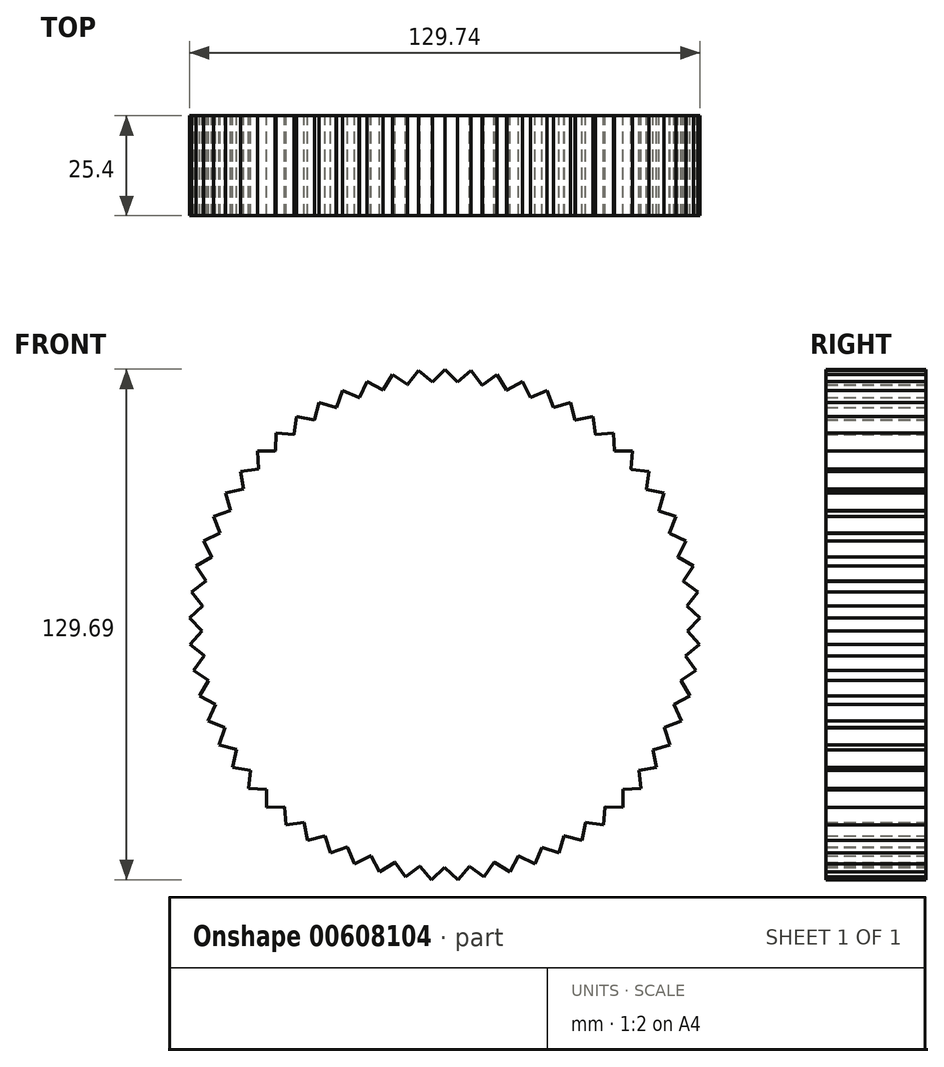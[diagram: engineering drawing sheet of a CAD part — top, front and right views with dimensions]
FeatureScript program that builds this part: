
annotation { "Feature Type Name" : "Feature", "Feature Type Description" : "" }
export const myFeature = defineFeature(function(context is Context, id is Id, definition is map)
    precondition{}
    {
        {
            var Q0;
            Q0=qCreatedBy(makeId("Front.planeOp"),FACE);
            var sketch = newSketch(context, id + "F0", { "sketchPlane" : qUnion([Q0])});
            skCircle(sketch, "E0", {"center": v(0, 0) * mm, "radius": 61.69 * mm});
            skPoint(sketch, "E1", {"position": v(0, -64.89) * mm});
            skPoint(sketch, "E2", {"position": v(65.93, 0) * mm});
            skPoint(sketch, "E3", {"position": v(-64.89, 0) * mm});
            skLineSegment(sketch, "E4", {"start": v(-3.17, 61.56) * mm, "end": v(0, 64.89) * mm});
            skLineSegment(sketch, "E5", {"start": v(0, 64.89) * mm, "end": v(3.18, 61.6) * mm});
            skLineSegment(sketch, "E6.1.0", {"start": v(-9.48, 60.9) * mm, "end": v(-6.67, 64.55) * mm});
            skLineSegment(sketch, "E6.1.1", {"start": v(-6.67, 64.55) * mm, "end": v(-3.17, 61.6) * mm});
            skLineSegment(sketch, "E6.2.0", {"start": v(-15.7, 59.6) * mm, "end": v(-13.27, 63.52) * mm});
            skLineSegment(sketch, "E6.2.1", {"start": v(-13.27, 63.52) * mm, "end": v(-9.5, 60.95) * mm});
            skLineSegment(sketch, "E6.3.0", {"start": v(-21.74, 57.68) * mm, "end": v(-19.73, 61.82) * mm});
            skLineSegment(sketch, "E6.3.1", {"start": v(-19.73, 61.82) * mm, "end": v(-15.7, 59.65) * mm});
            skLineSegment(sketch, "E6.4.0", {"start": v(-27.56, 55.14) * mm, "end": v(-25.98, 59.46) * mm});
            skLineSegment(sketch, "E6.4.1", {"start": v(-25.98, 59.46) * mm, "end": v(-21.76, 57.72) * mm});
            skLineSegment(sketch, "E6.5.0", {"start": v(-33.08, 52.01) * mm, "end": v(-31.96, 56.48) * mm});
            skLineSegment(sketch, "E6.5.1", {"start": v(-31.96, 56.48) * mm, "end": v(-27.58, 55.18) * mm});
            skLineSegment(sketch, "E6.6.0", {"start": v(-38.25, 48.33) * mm, "end": v(-37.6, 52.9) * mm});
            skLineSegment(sketch, "E6.6.1", {"start": v(-37.6, 52.9) * mm, "end": v(-33.1, 52.05) * mm});
            skLineSegment(sketch, "E6.7.0", {"start": v(-43.02, 44.14) * mm, "end": v(-42.83, 48.74) * mm});
            skLineSegment(sketch, "E6.7.1", {"start": v(-42.83, 48.74) * mm, "end": v(-38.28, 48.37) * mm});
            skLineSegment(sketch, "E6.8.0", {"start": v(-47.33, 39.49) * mm, "end": v(-47.62, 44.08) * mm});
            skLineSegment(sketch, "E6.8.1", {"start": v(-47.62, 44.08) * mm, "end": v(-43.05, 44.18) * mm});
            skLineSegment(sketch, "E6.9.0", {"start": v(-51.14, 34.41) * mm, "end": v(-51.9, 38.95) * mm});
            skLineSegment(sketch, "E6.9.1", {"start": v(-51.9, 38.95) * mm, "end": v(-47.37, 39.52) * mm});
            skLineSegment(sketch, "E6.10.0", {"start": v(-54.4, 28.97) * mm, "end": v(-55.63, 33.4) * mm});
            skLineSegment(sketch, "E6.10.1", {"start": v(-55.63, 33.4) * mm, "end": v(-51.18, 34.44) * mm});
            skLineSegment(sketch, "E6.11.0", {"start": v(-57.1, 23.22) * mm, "end": v(-58.77, 27.51) * mm});
            skLineSegment(sketch, "E6.11.1", {"start": v(-58.77, 27.51) * mm, "end": v(-54.45, 29) * mm});
            skLineSegment(sketch, "E6.12.0", {"start": v(-59.18, 17.23) * mm, "end": v(-61.29, 21.32) * mm});
            skLineSegment(sketch, "E6.12.1", {"start": v(-61.29, 21.32) * mm, "end": v(-57.14, 23.24) * mm});
            skLineSegment(sketch, "E6.13.0", {"start": v(-60.64, 11.05) * mm, "end": v(-63.15, 14.91) * mm});
            skLineSegment(sketch, "E6.13.1", {"start": v(-63.15, 14.91) * mm, "end": v(-59.23, 17.24) * mm});
            skLineSegment(sketch, "E6.14.0", {"start": v(-61.46, 4.76) * mm, "end": v(-64.35, 8.34) * mm});
            skLineSegment(sketch, "E6.14.1", {"start": v(-64.35, 8.34) * mm, "end": v(-60.69, 11.06) * mm});
            skLineSegment(sketch, "E6.15.0", {"start": v(-61.62, -1.59) * mm, "end": v(-64.87, 1.68) * mm});
            skLineSegment(sketch, "E6.15.1", {"start": v(-64.87, 1.68) * mm, "end": v(-61.5, 4.76) * mm});
            skLineSegment(sketch, "E6.16.0", {"start": v(-61.13, -7.91) * mm, "end": v(-64.7, -5) * mm});
            skLineSegment(sketch, "E6.16.1", {"start": v(-64.7, -5) * mm, "end": v(-61.67, -1.59) * mm});
            skLineSegment(sketch, "E6.17.0", {"start": v(-60, -14.16) * mm, "end": v(-63.84, -11.63) * mm});
            skLineSegment(sketch, "E6.17.1", {"start": v(-63.84, -11.63) * mm, "end": v(-61.18, -7.92) * mm});
            skLineSegment(sketch, "E6.18.0", {"start": v(-58.22, -20.25) * mm, "end": v(-62.3, -18.13) * mm});
            skLineSegment(sketch, "E6.18.1", {"start": v(-62.3, -18.13) * mm, "end": v(-60.04, -14.17) * mm});
            skLineSegment(sketch, "E6.19.0", {"start": v(-55.83, -26.13) * mm, "end": v(-60.11, -24.44) * mm});
            skLineSegment(sketch, "E6.19.1", {"start": v(-60.11, -24.44) * mm, "end": v(-58.26, -20.27) * mm});
            skLineSegment(sketch, "E6.20.0", {"start": v(-52.84, -31.73) * mm, "end": v(-57.28, -30.5) * mm});
            skLineSegment(sketch, "E6.20.1", {"start": v(-57.28, -30.5) * mm, "end": v(-55.87, -26.15) * mm});
            skLineSegment(sketch, "E6.21.0", {"start": v(-49.3, -37) * mm, "end": v(-53.84, -36.22) * mm});
            skLineSegment(sketch, "E6.21.1", {"start": v(-53.84, -36.22) * mm, "end": v(-52.89, -31.75) * mm});
            skLineSegment(sketch, "E6.22.0", {"start": v(-45.24, -41.87) * mm, "end": v(-49.83, -41.56) * mm});
            skLineSegment(sketch, "E6.22.1", {"start": v(-49.83, -41.56) * mm, "end": v(-49.34, -37.02) * mm});
            skLineSegment(sketch, "E6.23.0", {"start": v(-40.7, -46.3) * mm, "end": v(-45.3, -46.47) * mm});
            skLineSegment(sketch, "E6.23.1", {"start": v(-45.3, -46.47) * mm, "end": v(-45.27, -41.9) * mm});
            skLineSegment(sketch, "E6.24.0", {"start": v(-35.72, -50.24) * mm, "end": v(-40.28, -50.88) * mm});
            skLineSegment(sketch, "E6.24.1", {"start": v(-40.28, -50.88) * mm, "end": v(-40.72, -46.33) * mm});
            skLineSegment(sketch, "E6.25.0", {"start": v(-30.36, -53.64) * mm, "end": v(-34.83, -54.75) * mm});
            skLineSegment(sketch, "E6.25.1", {"start": v(-34.83, -54.75) * mm, "end": v(-35.74, -50.28) * mm});
            skLineSegment(sketch, "E6.26.0", {"start": v(-24.68, -56.48) * mm, "end": v(-29.02, -58.04) * mm});
            skLineSegment(sketch, "E6.26.1", {"start": v(-29.02, -58.04) * mm, "end": v(-30.39, -53.68) * mm});
            skLineSegment(sketch, "E6.27.0", {"start": v(-18.75, -58.72) * mm, "end": v(-22.9, -60.72) * mm});
            skLineSegment(sketch, "E6.27.1", {"start": v(-22.9, -60.72) * mm, "end": v(-24.7, -56.52) * mm});
            skLineSegment(sketch, "E6.28.0", {"start": v(-12.6, -60.34) * mm, "end": v(-16.53, -62.75) * mm});
            skLineSegment(sketch, "E6.28.1", {"start": v(-16.53, -62.75) * mm, "end": v(-18.76, -58.77) * mm});
            skLineSegment(sketch, "E6.29.0", {"start": v(-6.34, -61.31) * mm, "end": v(-10, -64.12) * mm});
            skLineSegment(sketch, "E6.29.1", {"start": v(-10, -64.12) * mm, "end": v(-12.62, -60.38) * mm});
            skLineSegment(sketch, "E6.30.0", {"start": v(0, -61.64) * mm, "end": v(-3.35, -64.8) * mm});
            skLineSegment(sketch, "E6.30.1", {"start": v(-3.35, -64.8) * mm, "end": v(-6.34, -61.36) * mm});
            skLineSegment(sketch, "E6.31.0", {"start": v(6.34, -61.31) * mm, "end": v(3.33, -64.8) * mm});
            skLineSegment(sketch, "E6.31.1", {"start": v(3.33, -64.8) * mm, "end": v(0, -61.69) * mm});
            skLineSegment(sketch, "E6.32.0", {"start": v(12.6, -60.34) * mm, "end": v(9.98, -64.12) * mm});
            skLineSegment(sketch, "E6.32.1", {"start": v(9.98, -64.12) * mm, "end": v(6.34, -61.36) * mm});
            skLineSegment(sketch, "E6.33.0", {"start": v(18.74, -58.72) * mm, "end": v(16.52, -62.75) * mm});
            skLineSegment(sketch, "E6.33.1", {"start": v(16.52, -62.75) * mm, "end": v(12.62, -60.38) * mm});
            skLineSegment(sketch, "E6.34.0", {"start": v(24.68, -56.48) * mm, "end": v(22.88, -60.72) * mm});
            skLineSegment(sketch, "E6.34.1", {"start": v(22.88, -60.72) * mm, "end": v(18.76, -58.77) * mm});
            skLineSegment(sketch, "E6.35.0", {"start": v(30.36, -53.64) * mm, "end": v(29, -58.05) * mm});
            skLineSegment(sketch, "E6.35.1", {"start": v(29, -58.05) * mm, "end": v(24.7, -56.53) * mm});
            skLineSegment(sketch, "E6.36.0", {"start": v(35.71, -50.24) * mm, "end": v(34.82, -54.76) * mm});
            skLineSegment(sketch, "E6.36.1", {"start": v(34.82, -54.76) * mm, "end": v(30.38, -53.69) * mm});
            skLineSegment(sketch, "E6.37.0", {"start": v(40.7, -46.3) * mm, "end": v(40.27, -50.88) * mm});
            skLineSegment(sketch, "E6.37.1", {"start": v(40.27, -50.88) * mm, "end": v(35.74, -50.28) * mm});
            skLineSegment(sketch, "E6.38.0", {"start": v(45.24, -41.87) * mm, "end": v(45.28, -46.47) * mm});
            skLineSegment(sketch, "E6.38.1", {"start": v(45.28, -46.47) * mm, "end": v(40.72, -46.34) * mm});
            skLineSegment(sketch, "E6.39.0", {"start": v(49.3, -37) * mm, "end": v(49.82, -41.57) * mm});
            skLineSegment(sketch, "E6.39.1", {"start": v(49.82, -41.57) * mm, "end": v(45.27, -41.9) * mm});
            skLineSegment(sketch, "E6.40.0", {"start": v(52.84, -31.73) * mm, "end": v(53.83, -36.23) * mm});
            skLineSegment(sketch, "E6.40.1", {"start": v(53.83, -36.23) * mm, "end": v(49.34, -37.03) * mm});
            skLineSegment(sketch, "E6.41.0", {"start": v(55.83, -26.13) * mm, "end": v(57.27, -30.5) * mm});
            skLineSegment(sketch, "E6.41.1", {"start": v(57.27, -30.5) * mm, "end": v(52.88, -31.76) * mm});
            skLineSegment(sketch, "E6.42.0", {"start": v(58.22, -20.25) * mm, "end": v(60.1, -24.45) * mm});
            skLineSegment(sketch, "E6.42.1", {"start": v(60.1, -24.45) * mm, "end": v(55.87, -26.15) * mm});
            skLineSegment(sketch, "E6.43.0", {"start": v(60, -14.16) * mm, "end": v(62.3, -18.14) * mm});
            skLineSegment(sketch, "E6.43.1", {"start": v(62.3, -18.14) * mm, "end": v(58.26, -20.27) * mm});
            skLineSegment(sketch, "E6.44.0", {"start": v(61.13, -7.92) * mm, "end": v(63.84, -11.64) * mm});
            skLineSegment(sketch, "E6.44.1", {"start": v(63.84, -11.64) * mm, "end": v(60.04, -14.17) * mm});
            skLineSegment(sketch, "E6.45.0", {"start": v(61.62, -1.59) * mm, "end": v(64.7, -5.01) * mm});
            skLineSegment(sketch, "E6.45.1", {"start": v(64.7, -5.01) * mm, "end": v(61.18, -7.92) * mm});
            skLineSegment(sketch, "E6.46.0", {"start": v(61.46, 4.76) * mm, "end": v(64.87, 1.66) * mm});
            skLineSegment(sketch, "E6.46.1", {"start": v(64.87, 1.66) * mm, "end": v(61.67, -1.6) * mm});
            skLineSegment(sketch, "E6.47.0", {"start": v(60.64, 11.05) * mm, "end": v(64.35, 8.33) * mm});
            skLineSegment(sketch, "E6.47.1", {"start": v(64.35, 8.33) * mm, "end": v(61.5, 4.76) * mm});
            skLineSegment(sketch, "E6.48.0", {"start": v(59.18, 17.23) * mm, "end": v(63.16, 14.9) * mm});
            skLineSegment(sketch, "E6.48.1", {"start": v(63.16, 14.9) * mm, "end": v(60.69, 11.06) * mm});
            skLineSegment(sketch, "E6.49.0", {"start": v(57.1, 23.22) * mm, "end": v(61.29, 21.31) * mm});
            skLineSegment(sketch, "E6.49.1", {"start": v(61.29, 21.31) * mm, "end": v(59.23, 17.24) * mm});
            skLineSegment(sketch, "E6.50.0", {"start": v(54.4, 28.97) * mm, "end": v(58.77, 27.5) * mm});
            skLineSegment(sketch, "E6.50.1", {"start": v(58.77, 27.5) * mm, "end": v(57.14, 23.24) * mm});
            skLineSegment(sketch, "E6.51.0", {"start": v(51.14, 34.4) * mm, "end": v(55.63, 33.4) * mm});
            skLineSegment(sketch, "E6.51.1", {"start": v(55.63, 33.4) * mm, "end": v(54.45, 28.99) * mm});
            skLineSegment(sketch, "E6.52.0", {"start": v(47.33, 39.49) * mm, "end": v(51.9, 38.94) * mm});
            skLineSegment(sketch, "E6.52.1", {"start": v(51.9, 38.94) * mm, "end": v(51.18, 34.44) * mm});
            skLineSegment(sketch, "E6.53.0", {"start": v(43.02, 44.14) * mm, "end": v(47.63, 44.07) * mm});
            skLineSegment(sketch, "E6.53.1", {"start": v(47.63, 44.07) * mm, "end": v(47.37, 39.52) * mm});
            skLineSegment(sketch, "E6.54.0", {"start": v(38.25, 48.33) * mm, "end": v(42.84, 48.74) * mm});
            skLineSegment(sketch, "E6.54.1", {"start": v(42.84, 48.74) * mm, "end": v(43.06, 44.18) * mm});
            skLineSegment(sketch, "E6.55.0", {"start": v(33.08, 52) * mm, "end": v(37.6, 52.88) * mm});
            skLineSegment(sketch, "E6.55.1", {"start": v(37.6, 52.88) * mm, "end": v(38.29, 48.37) * mm});
            skLineSegment(sketch, "E6.56.0", {"start": v(27.56, 55.14) * mm, "end": v(31.97, 56.47) * mm});
            skLineSegment(sketch, "E6.56.1", {"start": v(31.97, 56.47) * mm, "end": v(33.1, 52.05) * mm});
            skLineSegment(sketch, "E6.57.0", {"start": v(21.74, 57.68) * mm, "end": v(26, 59.46) * mm});
            skLineSegment(sketch, "E6.57.1", {"start": v(26, 59.46) * mm, "end": v(27.58, 55.18) * mm});
            skLineSegment(sketch, "E6.58.0", {"start": v(15.7, 59.6) * mm, "end": v(19.74, 61.81) * mm});
            skLineSegment(sketch, "E6.58.1", {"start": v(19.74, 61.81) * mm, "end": v(21.76, 57.72) * mm});
            skLineSegment(sketch, "E6.59.0", {"start": v(9.49, 60.9) * mm, "end": v(13.28, 63.52) * mm});
            skLineSegment(sketch, "E6.59.1", {"start": v(13.28, 63.52) * mm, "end": v(15.71, 59.65) * mm});
            skLineSegment(sketch, "E6.60.0", {"start": v(3.17, 61.56) * mm, "end": v(6.68, 64.54) * mm});
            skLineSegment(sketch, "E6.60.1", {"start": v(6.68, 64.54) * mm, "end": v(9.5, 60.95) * mm});
            skSolve(sketch);
        }
        {
            var Q0;
            Q0 = qSketchRegion(id + "F0", true);
            extrude(context, id + "F1", {"entities" : qUnion([Q0]), "depth" : 25.4 * mm, "offsetDistance" : 25.4 * mm});
        }
    });
